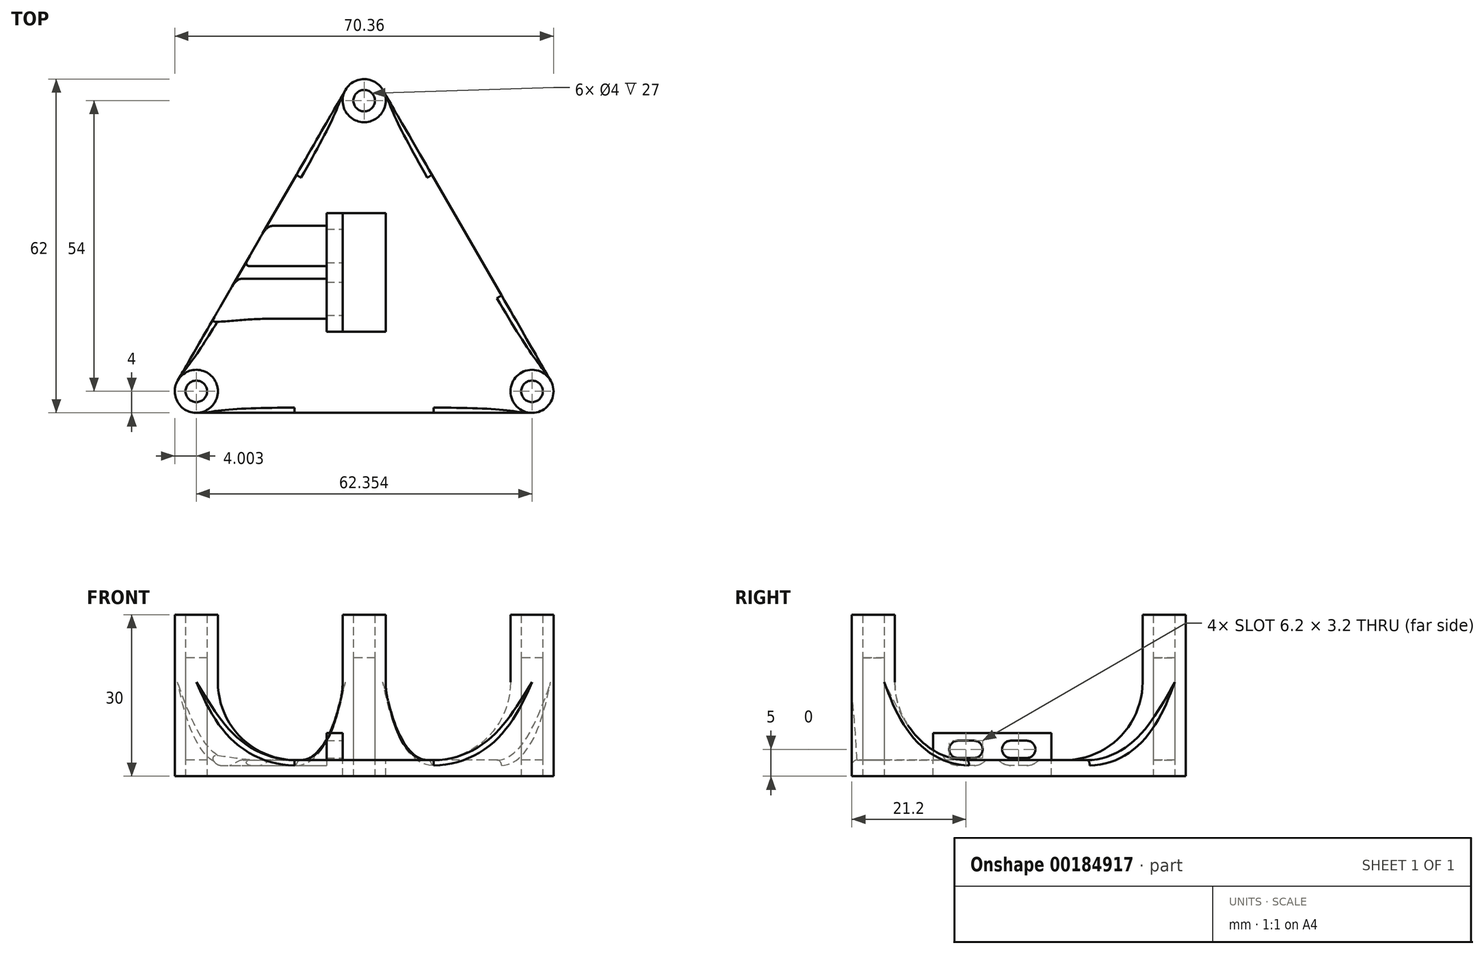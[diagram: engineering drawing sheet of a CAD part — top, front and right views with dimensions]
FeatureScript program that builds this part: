
annotation { "Feature Type Name" : "Feature", "Feature Type Description" : "" }
export const myFeature = defineFeature(function(context is Context, id is Id, definition is map)
    precondition{}
    {
        {
            var Q0;
            Q0=qCreatedBy(makeId("Top.planeOp"),FACE);
            var sketch = newSketch(context, id + "F0", { "sketchPlane" : qUnion([Q0])});
            skCircle(sketch, "E0", {"center": v(-31.18, 0) * mm, "radius": 2 * mm});
            skCircle(sketch, "E1", {"center": v(-31.18, 0) * mm, "radius": 4 * mm});
            skCircle(sketch, "E2", {"center": v(31.18, 0) * mm, "radius": 4 * mm});
            skCircle(sketch, "E3", {"center": v(31.18, 0) * mm, "radius": 2 * mm});
            skPoint(sketch, "E4", {"position": v(0, 0) * mm});
            skCircle(sketch, "E5", {"center": v(0, 54) * mm, "radius": 2 * mm});
            skCircle(sketch, "E6", {"center": v(0, 54) * mm, "radius": 4 * mm});
            skLineSegment(sketch, "E7.trimOffspring", {"start": v(2, 50.54) * mm, "end": v(29.18, 3.46) * mm});
            skLineSegment(sketch, "E8.trimOffspring", {"start": v(-29.18, 3.46) * mm, "end": v(-2, 50.54) * mm});
            skLineSegment(sketch, "E9.trimOffspring", {"start": v(-27.18, 0) * mm, "end": v(27.18, 0) * mm});
            skSolve(sketch);
        }
        {
            var Q0;
            Q0=makeQuery(id+"F0.imprint","IMPRINT",FACE,{"disambiguationData":[TD([[makeQuery(id+"F0.imprint","IMPRINT",EDGE,{"derivedFrom":sQuery(id+"F0.wireOp",EDGE,"E5")}),-1.0]])]});
            var Q1;
            Q1=makeQuery(id+"F0.imprint","IMPRINT",FACE,{"disambiguationData":[TD([[makeQuery(id+"F0.imprint","IMPRINT",EDGE,{"derivedFrom":sQuery(id+"F0.wireOp",EDGE,"E0")}),-1.0]])]});
            var Q2;
            Q2=makeQuery(id+"F0.imprint","IMPRINT",FACE,{"disambiguationData":[TD([[makeQuery(id+"F0.imprint","IMPRINT",EDGE,{"derivedFrom":sQuery(id+"F0.wireOp",EDGE,"E3")}),-1.0]])]});
            extrude(context, id + "F1", {"entities" : qUnion([Q0, Q1, Q2]), "depth" : 30 * mm});
        }
        {
            var Q0;
            Q0=qCreatedBy(makeId("Top.planeOp"),FACE);
            var sketch = newSketch(context, id + "F2", { "sketchPlane" : qUnion([Q0])});
            skCircle(sketch, "E10", {"center": v(-31.18, 0) * mm, "radius": 2 * mm});
            skCircle(sketch, "E11", {"center": v(31.18, 0) * mm, "radius": 2 * mm});
            skCircle(sketch, "E12", {"center": v(0, 54) * mm, "radius": 2 * mm});
            skSolve(sketch);
        }
        {
            var Q0;
            Q0=makeQuery(id+"F2.imprint","IMPRINT",FACE,{"disambiguationData":[TD([[makeQuery(id+"F2.imprint","IMPRINT",EDGE,{"derivedFrom":sQuery(id+"F2.wireOp",EDGE,"E10")}),1.0]])]});
            var Q1;
            Q1=makeQuery(id+"F2.imprint","IMPRINT",FACE,{"disambiguationData":[TD([[makeQuery(id+"F2.imprint","IMPRINT",EDGE,{"derivedFrom":sQuery(id+"F2.wireOp",EDGE,"E11")}),1.0]])]});
            var Q2;
            Q2=makeQuery(id+"F2.imprint","IMPRINT",FACE,{"disambiguationData":[TD([[makeQuery(id+"F2.imprint","IMPRINT",EDGE,{"derivedFrom":sQuery(id+"F2.wireOp",EDGE,"E12")}),1.0]])]});
            extrude(context, id + "F3", {"entities" : qUnion([Q0, Q1, Q2]), "depth" : (30 - 8) * mm});
        }
        {
            var Q0;
            Q0=qCreatedBy(makeId("Top.planeOp"),FACE);
            var sketch = newSketch(context, id + "F4", { "sketchPlane" : qUnion([Q0])});
            skLineSegment(sketch, "E13", {"start": v(-34.64, 2) * mm, "end": v(-3.46, 56) * mm});
            skLineSegment(sketch, "E14", {"start": v(-31.18, -4) * mm, "end": v(31.18, -4) * mm});
            skLineSegment(sketch, "E15", {"start": v(34.64, 2) * mm, "end": v(3.46, 56) * mm});
            skArc(sketch, "E16", {"start": v(-34.64, 2) * mm, "mid": v(-34.64, -2) * mm, "end": v(-31.18, -4) * mm});
            skArc(sketch, "E17", {"start": v(31.18, -4) * mm, "mid": v(34.64, -2) * mm, "end": v(34.64, 2) * mm});
            skArc(sketch, "E18", {"start": v(3.46, 56) * mm, "mid": v(0, 58) * mm, "end": v(-3.46, 56) * mm});
            skSolve(sketch);
        }
        {
            var Q0;
            Q0=makeQuery(id+"F4.imprint","IMPRINT",FACE,{"disambiguationData":[TD([[makeQuery(id+"F4.imprint","IMPRINT",EDGE,{"derivedFrom":sQuery(id+"F4.wireOp",EDGE,"E13")}),-1.0]])]});
            extrude(context, id + "F5", {"entities" : qUnion([Q0]), "depth" : 3 * mm});
        }
        {
            var Q0;
            Q0=makeQuery(id+"F1.opExtrude","SWEPT_BODY",BODY,{"disambiguationData":[OSD([sQuery(id+"F0.wireOp",EDGE,"E0"),sQuery(id+"F0.wireOp",EDGE,"E1")])]});
            var Q1;
            Q1=makeQuery(id+"F1.opExtrude","SWEPT_BODY",BODY,{"disambiguationData":[OSD([sQuery(id+"F0.wireOp",EDGE,"E2"),sQuery(id+"F0.wireOp",EDGE,"E3")])]});
            var Q2;
            Q2=makeQuery(id+"F1.opExtrude","SWEPT_BODY",BODY,{"disambiguationData":[OSD([sQuery(id+"F0.wireOp",EDGE,"E5"),sQuery(id+"F0.wireOp",EDGE,"E6")])]});
            var Q3;
            Q3=makeQuery(id+"F5.opExtrude","SWEPT_BODY",BODY,{"disambiguationData":[OSD([sQuery(id+"F4.wireOp",EDGE,"E13"),sQuery(id+"F4.wireOp",EDGE,"E14"),sQuery(id+"F4.wireOp",EDGE,"E15"),sQuery(id+"F4.wireOp",EDGE,"E16"),sQuery(id+"F4.wireOp",EDGE,"E17"),sQuery(id+"F4.wireOp",EDGE,"E18")])]});
            booleanBodies(context, id + "F6", {"operationType" : BooleanOperationType.UNION, "tools" : qUnion([Q0, Q1, Q2, Q3])});
        }
        {
            var Q0;
            Q0=makeQuery(id+"F5.opExtrude","CAP_FACE",FACE,{"disambiguationData":[OSD([sQuery(id+"F4.wireOp",EDGE,"E13"),sQuery(id+"F4.wireOp",EDGE,"E14"),sQuery(id+"F4.wireOp",EDGE,"E15"),sQuery(id+"F4.wireOp",EDGE,"E16"),sQuery(id+"F4.wireOp",EDGE,"E17"),sQuery(id+"F4.wireOp",EDGE,"E18")])],"isStart":false});
            var sketch = newSketch(context, id + "F7", { "sketchPlane" : qUnion([Q0])});
            skLineSegment(sketch, "E19.bottom", {"start": v(-4, 33.1) * mm, "end": v(4, 33.1) * mm});
            skLineSegment(sketch, "E19.top", {"start": v(-4, 11.1) * mm, "end": v(4, 11.1) * mm});
            skLineSegment(sketch, "E19.left", {"start": v(-4, 33.1) * mm, "end": v(-4, 11.1) * mm});
            skLineSegment(sketch, "E19.right", {"start": v(4, 33.1) * mm, "end": v(4, 11.1) * mm});
            skCircle(sketch, "E20", {"center": v(0, 18) * mm, "radius": 36 * mm});
            skPoint(sketch, "E21", {"position": v(0, 54) * mm});
            skPoint(sketch, "E22", {"position": v(-31.18, 0) * mm});
            skPoint(sketch, "E23", {"position": v(31.18, 0) * mm});
            skPoint(sketch, "E24", {"position": v(-4, 18) * mm});
            skPoint(sketch, "E25", {"position": v(0, 33.1) * mm});
            skSolve(sketch);
        }
        {
            var Q0;
            Q0=makeQuery(id+"F7.imprint","IMPRINT",FACE,{"disambiguationData":[TD([[makeQuery(id+"F7.imprint","IMPRINT",EDGE,{"derivedFrom":sQuery(id+"F7.wireOp",EDGE,"E19.bottom")}),-1.0]])]});
            extrude(context, id + "F8", {"entities" : qUnion([Q0]), "operationType" : NewBodyOperationType.REMOVE, "endBound" : BoundingType.THROUGH_ALL, "oppositeDirection" : true, "depth" : 25 * mm});
        }
        {
            var Q0;
            Q0=makeQuery(id+"F5.opExtrude","CAP_FACE",FACE,{"disambiguationData":[OSD([sQuery(id+"F4.wireOp",EDGE,"E13"),sQuery(id+"F4.wireOp",EDGE,"E14"),sQuery(id+"F4.wireOp",EDGE,"E15"),sQuery(id+"F4.wireOp",EDGE,"E16"),sQuery(id+"F4.wireOp",EDGE,"E17"),sQuery(id+"F4.wireOp",EDGE,"E18")])],"isStart":false});
            var sketch = newSketch(context, id + "F9", { "sketchPlane" : qUnion([Q0])});
            skLineSegment(sketch, "E26.bottom", {"start": v(-4, 33.1) * mm, "end": v(-7, 33.1) * mm});
            skLineSegment(sketch, "E26.top", {"start": v(-4, 11.1) * mm, "end": v(-7, 11.1) * mm});
            skLineSegment(sketch, "E26.left", {"start": v(-4, 33.1) * mm, "end": v(-4, 11.1) * mm});
            skLineSegment(sketch, "E26.right", {"start": v(-7, 33.1) * mm, "end": v(-7, 11.1) * mm});
            skSolve(sketch);
        }
        {
            var Q0;
            Q0=makeQuery(id+"F9.imprint","IMPRINT",FACE,{"disambiguationData":[TD([[makeQuery(id+"F9.imprint","IMPRINT",EDGE,{"derivedFrom":sQuery(id+"F9.wireOp",EDGE,"E26.bottom")}),1.0]])]});
            extrude(context, id + "F10", {"entities" : qUnion([Q0]), "depth" : (3 + 2) * mm});
        }
        {
            var Q0;
            Q0=makeQuery(id+"F1.opExtrude","SWEPT_BODY",BODY,{"disambiguationData":[OSD([sQuery(id+"F0.wireOp",EDGE,"E0"),sQuery(id+"F0.wireOp",EDGE,"E1")])]});
            var Q1;
            Q1=makeQuery(id+"F10.opExtrude","SWEPT_BODY",BODY,{"disambiguationData":[OSD([sQuery(id+"F9.wireOp",EDGE,"E26.bottom"),sQuery(id+"F9.wireOp",EDGE,"E26.top"),sQuery(id+"F9.wireOp",EDGE,"E26.left"),sQuery(id+"F9.wireOp",EDGE,"E26.right")])]});
            booleanBodies(context, id + "F11", {"operationType" : BooleanOperationType.UNION, "tools" : qUnion([Q0, Q1])});
        }
        {
            var Q0;
            Q0=makeQuery(id+"F11.opBoolean","MERGE",FACE,{"derivedFrom":[makeQuery(id+"F8.boolean.opBoolean","COPY",FACE,{"derivedFrom":makeQuery(id+"F8.opExtrude","SWEPT_FACE",FACE,{"disambiguationData":[OSD([sQuery(id+"F7.wireOp",EDGE,"E19.left")])]})}),makeQuery(id+"F10.opExtrude","SWEPT_FACE",FACE,{"disambiguationData":[OSD([sQuery(id+"F9.wireOp",EDGE,"E26.left")])]})]});
            var sketch = newSketch(context, id + "F12", { "sketchPlane" : qUnion([Q0])});
            skArc(sketch, "E27", {"start": v(15.7, 6.6) * mm, "mid": v(14.1, 5) * mm, "end": v(15.7, 3.4) * mm});
            skArc(sketch, "E28", {"start": v(25.5, 6.6) * mm, "mid": v(23.9, 5) * mm, "end": v(25.5, 3.4) * mm});
            skArc(sketch, "E29", {"start": v(18.7, 3.4) * mm, "mid": v(20.3, 5) * mm, "end": v(18.7, 6.6) * mm});
            skArc(sketch, "E30", {"start": v(28.5, 3.4) * mm, "mid": v(30.1, 5) * mm, "end": v(28.5, 6.6) * mm});
            skLineSegment(sketch, "E31", {"start": v(15.7, 6.6) * mm, "end": v(18.7, 6.6) * mm});
            skLineSegment(sketch, "E32", {"start": v(15.7, 3.4) * mm, "end": v(18.7, 3.4) * mm});
            skLineSegment(sketch, "E33", {"start": v(25.5, 6.6) * mm, "end": v(28.5, 6.6) * mm});
            skLineSegment(sketch, "E34", {"start": v(25.5, 3.4) * mm, "end": v(28.5, 3.4) * mm});
            skSolve(sketch);
        }
        {
            var Q0;
            Q0=makeQuery(id+"F12.imprint","IMPRINT",FACE,{"disambiguationData":[TD([[makeQuery(id+"F12.imprint","IMPRINT",EDGE,{"derivedFrom":sQuery(id+"F12.wireOp",EDGE,"E27")}),1.0]])]});
            var Q1;
            Q1=makeQuery(id+"F12.imprint","IMPRINT",FACE,{"disambiguationData":[TD([[makeQuery(id+"F12.imprint","IMPRINT",EDGE,{"derivedFrom":sQuery(id+"F12.wireOp",EDGE,"E28")}),1.0]])]});
            extrude(context, id + "F13", {"entities" : qUnion([Q0, Q1]), "operationType" : NewBodyOperationType.REMOVE, "endBound" : BoundingType.THROUGH_ALL, "oppositeDirection" : true, "depth" : 25 * mm});
        }
        {
            var Q0;
            Q0=makeQuery(id+"F10.opExtrude","SWEPT_FACE",FACE,{"disambiguationData":[OSD([sQuery(id+"F9.wireOp",EDGE,"E26.right")])]});
            var sketch = newSketch(context, id + "F14", { "sketchPlane" : qUnion([Q0])});
            skArc(sketch, "E35", {"start": v(-25.5, 2) * mm, "mid": v(-22.5, 5) * mm, "end": v(-25.5, 8) * mm});
            skArc(sketch, "E36", {"start": v(-18.7, 8) * mm, "mid": v(-21.7, 5) * mm, "end": v(-18.7, 2) * mm});
            skLineSegment(sketch, "E37", {"start": v(-28.5, 8) * mm, "end": v(-25.5, 8) * mm});
            skLineSegment(sketch, "E38", {"start": v(-18.7, 8) * mm, "end": v(-15.7, 8) * mm});
            skLineSegment(sketch, "E39", {"start": v(-18.7, 2) * mm, "end": v(-15.7, 2) * mm});
            skLineSegment(sketch, "E40", {"start": v(-28.5, 2) * mm, "end": v(-25.5, 2) * mm});
            skArc(sketch, "E41.trimOffspring", {"start": v(-28.5, 8) * mm, "mid": v(-31.5, 5) * mm, "end": v(-28.5, 2) * mm});
            skArc(sketch, "E42.trimOffspring", {"start": v(-15.7, 2) * mm, "mid": v(-12.7, 5) * mm, "end": v(-15.7, 8) * mm});
            skSolve(sketch);
        }
        {
            var Q0;
            Q0=qSketchRegion(id+"F14",true);
            extrude(context, id + "F15", {"entities" : qUnion([Q0]), "operationType" : NewBodyOperationType.REMOVE, "depth" : 25 * mm});
        }
        {
            var Q0;
            Q0=makeQuery(id+"F6.opBoolean","INTERSECT",EDGE,{"derivedFrom":[makeQuery(id+"F1.opExtrude","SWEPT_FACE",FACE,{"disambiguationData":[OSD([sQuery(id+"F0.wireOp",EDGE,"E2")])]}),makeQuery(id+"F5.opExtrude","CAP_FACE",FACE,{"disambiguationData":[OSD([sQuery(id+"F4.wireOp",EDGE,"E13"),sQuery(id+"F4.wireOp",EDGE,"E14"),sQuery(id+"F4.wireOp",EDGE,"E15"),sQuery(id+"F4.wireOp",EDGE,"E16"),sQuery(id+"F4.wireOp",EDGE,"E17"),sQuery(id+"F4.wireOp",EDGE,"E18")])],"isStart":false})]});
            var Q1;
            Q1=makeQuery(id+"F6.opBoolean","INTERSECT",EDGE,{"derivedFrom":[makeQuery(id+"F1.opExtrude","SWEPT_FACE",FACE,{"disambiguationData":[OSD([sQuery(id+"F0.wireOp",EDGE,"E1")])]}),makeQuery(id+"F5.opExtrude","CAP_FACE",FACE,{"disambiguationData":[OSD([sQuery(id+"F4.wireOp",EDGE,"E13"),sQuery(id+"F4.wireOp",EDGE,"E14"),sQuery(id+"F4.wireOp",EDGE,"E15"),sQuery(id+"F4.wireOp",EDGE,"E16"),sQuery(id+"F4.wireOp",EDGE,"E17"),sQuery(id+"F4.wireOp",EDGE,"E18")])],"isStart":false})]});
            var Q2;
            Q2=makeQuery(id+"F6.opBoolean","INTERSECT",EDGE,{"derivedFrom":[makeQuery(id+"F1.opExtrude","SWEPT_FACE",FACE,{"disambiguationData":[OSD([sQuery(id+"F0.wireOp",EDGE,"E6")])]}),makeQuery(id+"F5.opExtrude","CAP_FACE",FACE,{"disambiguationData":[OSD([sQuery(id+"F4.wireOp",EDGE,"E13"),sQuery(id+"F4.wireOp",EDGE,"E14"),sQuery(id+"F4.wireOp",EDGE,"E15"),sQuery(id+"F4.wireOp",EDGE,"E16"),sQuery(id+"F4.wireOp",EDGE,"E17"),sQuery(id+"F4.wireOp",EDGE,"E18")])],"isStart":false})]});
            fillet(context, id + "F16", {"entities" : qUnion([Q0, Q1, Q2]), "radius" : 14.5 * mm, "tangentPropagation" : true, "allowEdgeOverflow" : false});
        }
        {
            var Q0;
            Q0=makeQuery(id+"F5.opExtrude","CAP_EDGE",EDGE,{"disambiguationData":[OSD([sQuery(id+"F4.wireOp",EDGE,"E14")])],"isStart":false});
            var Q1;
            {var subQ0=sQuery(id+"F4.wireOp",EDGE,"E13");Q1=makeQuery(id+"F15.boolean.opBoolean","SPLIT",EDGE,{"disambiguationData":[TD([makeQuery(id+"F1.opExtrude","SWEPT_FACE",FACE,{"disambiguationData":[OSD([sQuery(id+"F0.wireOp",EDGE,"E6")])]})])],"derivedFrom":makeQuery(id+"F5.opExtrude","CAP_EDGE",EDGE,{"disambiguationData":[OSD([subQ0])],"isStart":false})});}
            var Q2;
            {var subQ0=sQuery(id+"F4.wireOp",EDGE,"E13");Q2=makeQuery(id+"F16.opFillet","BLEND_EDGE",EDGE,{"blendedFrom":[makeQuery(id+"F6.opBoolean","INTERSECT",EDGE,{"derivedFrom":[makeQuery(id+"F1.opExtrude","SWEPT_FACE",FACE,{"disambiguationData":[OSD([sQuery(id+"F0.wireOp",EDGE,"E1")])]}),makeQuery(id+"F5.opExtrude","CAP_FACE",FACE,{"disambiguationData":[OSD([subQ0,sQuery(id+"F4.wireOp",EDGE,"E14"),sQuery(id+"F4.wireOp",EDGE,"E15"),sQuery(id+"F4.wireOp",EDGE,"E16"),sQuery(id+"F4.wireOp",EDGE,"E17"),sQuery(id+"F4.wireOp",EDGE,"E18")])],"isStart":false})]}),makeQuery(id+"F5.opExtrude","SWEPT_FACE",FACE,{"disambiguationData":[OSD([subQ0])]})],"blendedInto":[makeQuery(id+"F5.opExtrude","SWEPT_FACE",FACE,{"disambiguationData":[OSD([subQ0])]})]});}
            var Q3;
            {var subQ0=sQuery(id+"F4.wireOp",EDGE,"E13");Q3=makeQuery(id+"F15.boolean.opBoolean","SPLIT",EDGE,{"disambiguationData":[TD([makeQuery(id+"F15.opExtrude","SWEPT_FACE",FACE,{"disambiguationData":[OSD([sQuery(id+"F14.wireOp",EDGE,"E35")])]})])],"derivedFrom":makeQuery(id+"F5.opExtrude","CAP_EDGE",EDGE,{"disambiguationData":[OSD([subQ0])],"isStart":false})});}
            var Q4;
            Q4=makeQuery(id+"F5.opExtrude","CAP_EDGE",EDGE,{"disambiguationData":[OSD([sQuery(id+"F4.wireOp",EDGE,"E15")])],"isStart":false});
            fillet(context, id + "F17", {"entities" : qUnion([Q0, Q1, Q2, Q3, Q4]), "radius" : 1 * mm, "tangentPropagation" : true, "allowEdgeOverflow" : false});
        }
    });
